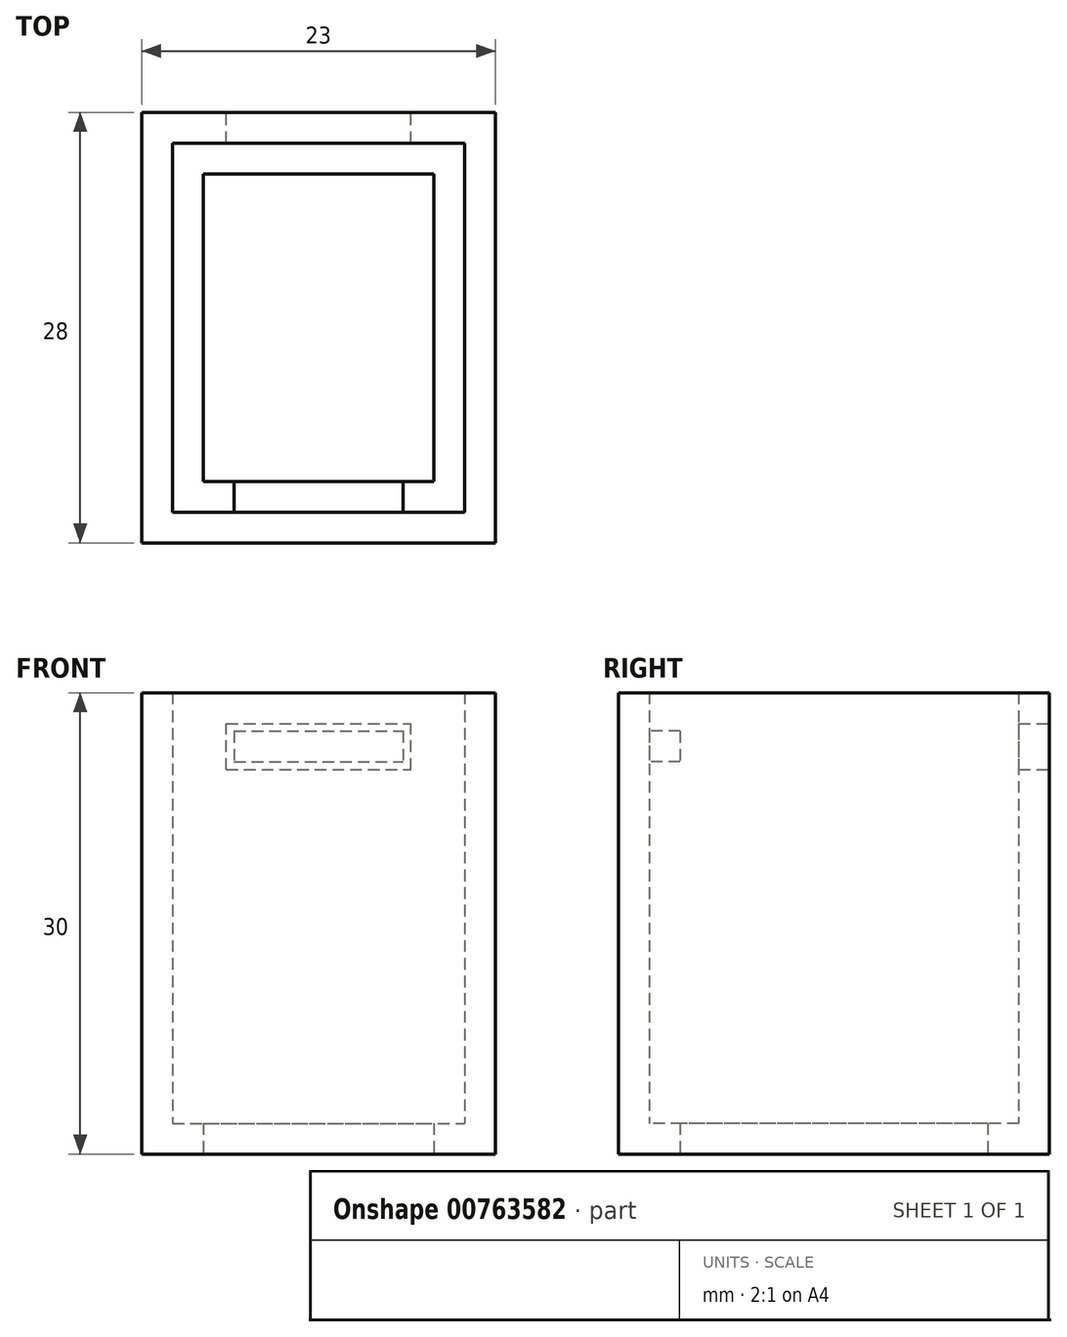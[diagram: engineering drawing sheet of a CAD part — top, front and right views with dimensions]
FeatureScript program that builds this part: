
annotation { "Feature Type Name" : "Feature", "Feature Type Description" : "" }
export const myFeature = defineFeature(function(context is Context, id is Id, definition is map)
    precondition{}
    {
        {
            var Q0;
            Q0=qCreatedBy(makeId("Top.planeOp"),FACE);
            var sketch = newSketch(context, id + "F0", { "sketchPlane" : qUnion([Q0])});
            skLineSegment(sketch, "E0.bottom", {"start": v(7.5, -10) * mm, "end": v(-7.5, -10) * mm});
            skLineSegment(sketch, "E0.top", {"start": v(7.5, 10) * mm, "end": v(-7.5, 10) * mm});
            skLineSegment(sketch, "E0.left", {"start": v(7.5, -10) * mm, "end": v(7.5, 10) * mm});
            skLineSegment(sketch, "E0.right", {"start": v(-7.5, -10) * mm, "end": v(-7.5, 10) * mm});
            skPoint(sketch, "E0.middle", {"position": v(0, 0) * mm});
            skLineSegment(sketch, "E1.0", {"start": v(9.5, 12) * mm, "end": v(-9.5, 12) * mm});
            skLineSegment(sketch, "E1.1", {"start": v(9.5, -12) * mm, "end": v(9.5, 12) * mm});
            skLineSegment(sketch, "E1.2", {"start": v(9.5, -12) * mm, "end": v(-9.5, -12) * mm});
            skLineSegment(sketch, "E1.3", {"start": v(-9.5, -12) * mm, "end": v(-9.5, 12) * mm});
            skLineSegment(sketch, "E2.0", {"start": v(11.5, -14) * mm, "end": v(-11.5, -14) * mm});
            skLineSegment(sketch, "E2.1", {"start": v(11.5, -14) * mm, "end": v(11.5, 14) * mm});
            skLineSegment(sketch, "E2.2", {"start": v(11.5, 14) * mm, "end": v(-11.5, 14) * mm});
            skLineSegment(sketch, "E2.3", {"start": v(-11.5, -14) * mm, "end": v(-11.5, 14) * mm});
            skSolve(sketch);
        }
        {
            var Q0;
            Q0=makeQuery(id+"F0.imprint","IMPRINT",FACE,{"disambiguationData":[TD([[makeQuery(id+"F0.imprint","IMPRINT",EDGE,{"derivedFrom":sQuery(id+"F0.wireOp",EDGE,"E1.0")}),-1.0]])]});
            var Q1;
            Q1=makeQuery(id+"F0.imprint","IMPRINT",FACE,{"disambiguationData":[TD([[makeQuery(id+"F0.imprint","IMPRINT",EDGE,{"derivedFrom":sQuery(id+"F0.wireOp",EDGE,"E0.bottom")}),1.0]])]});
            var Q2;
            Q2=makeQuery(id+"F0.imprint","IMPRINT",FACE,{"disambiguationData":[TD([[makeQuery(id+"F0.imprint","IMPRINT",EDGE,{"derivedFrom":sQuery(id+"F0.wireOp",EDGE,"E0.bottom")}),-1.0]])]});
            extrude(context, id + "F1", {"entities" : qUnion([Q0, Q1, Q2]), "depth" : 2 * mm, "offsetDistance" : 25 * mm});
        }
        {
            var Q0;
            Q0=makeQuery(id+"F0.imprint","IMPRINT",FACE,{"disambiguationData":[TD([[makeQuery(id+"F0.imprint","IMPRINT",EDGE,{"derivedFrom":sQuery(id+"F0.wireOp",EDGE,"E0.bottom")}),-1.0]])]});
            extrude(context, id + "F2", {"entities" : qUnion([Q0]), "operationType" : NewBodyOperationType.REMOVE, "depth" : 25 * mm, "offsetDistance" : 25 * mm});
        }
        {
            var Q0;
            Q0=makeQuery(id+"F0.imprint","IMPRINT",FACE,{"disambiguationData":[TD([[makeQuery(id+"F0.imprint","IMPRINT",EDGE,{"derivedFrom":sQuery(id+"F0.wireOp",EDGE,"E1.0")}),-1.0]])]});
            extrude(context, id + "F3", {"entities" : qUnion([Q0]), "operationType" : NewBodyOperationType.ADD, "depth" : 30 * mm, "offsetDistance" : 25 * mm});
        }
        {
            var Q0;
            {var subQ0=sQuery(id+"F0.wireOp",EDGE,"E2.2");Q0=makeQuery(id+"F3.boolean.opBoolean","MERGE",FACE,{"derivedFrom":[makeQuery(id+"F1.opExtrude","SWEPT_FACE",FACE,{"disambiguationData":[OSD([subQ0])]}),makeQuery(id+"F3.opExtrude","SWEPT_FACE",FACE,{"disambiguationData":[OSD([subQ0])]})]});}
            var sketch = newSketch(context, id + "F4", { "sketchPlane" : qUnion([Q0])});
            skLineSegment(sketch, "E3.bottom", {"start": v(6, 25) * mm, "end": v(-6, 25) * mm});
            skLineSegment(sketch, "E3.top", {"start": v(6, 28) * mm, "end": v(-6, 28) * mm});
            skLineSegment(sketch, "E3.left", {"start": v(6, 25) * mm, "end": v(6, 28) * mm});
            skLineSegment(sketch, "E3.right", {"start": v(-6, 25) * mm, "end": v(-6, 28) * mm});
            skPoint(sketch, "E3.middle", {"position": v(0, 26.5) * mm});
            skSolve(sketch);
        }
        {
            var Q0;
            Q0 = qSketchRegion(id + "F4", true);
            extrude(context, id + "F5", {"entities" : qUnion([Q0]), "operationType" : NewBodyOperationType.REMOVE, "oppositeDirection" : true, "depth" : 5 * mm, "offsetDistance" : 25 * mm});
        }
        {
            var Q0;
            Q0=makeQuery(id+"F3.opExtrude","SWEPT_FACE",FACE,{"disambiguationData":[OSD([sQuery(id+"F0.wireOp",EDGE,"E1.2")])]});
            var sketch = newSketch(context, id + "F6", { "sketchPlane" : qUnion([Q0])});
            skLineSegment(sketch, "E4.bottom", {"start": v(5.5, 27.5) * mm, "end": v(-5.5, 27.5) * mm});
            skLineSegment(sketch, "E4.top", {"start": v(5.5, 25.5) * mm, "end": v(-5.5, 25.5) * mm});
            skLineSegment(sketch, "E4.left", {"start": v(5.5, 27.5) * mm, "end": v(5.5, 25.5) * mm});
            skLineSegment(sketch, "E4.right", {"start": v(-5.5, 27.5) * mm, "end": v(-5.5, 25.5) * mm});
            skPoint(sketch, "E4.middle", {"position": v(0, 26.5) * mm});
            skSolve(sketch);
        }
        {
            var Q0;
            Q0 = qSketchRegion(id + "F6", true);
            extrude(context, id + "F7", {"entities" : qUnion([Q0]), "operationType" : NewBodyOperationType.ADD, "depth" : 2 * mm, "offsetDistance" : 25 * mm});
        }
    });
